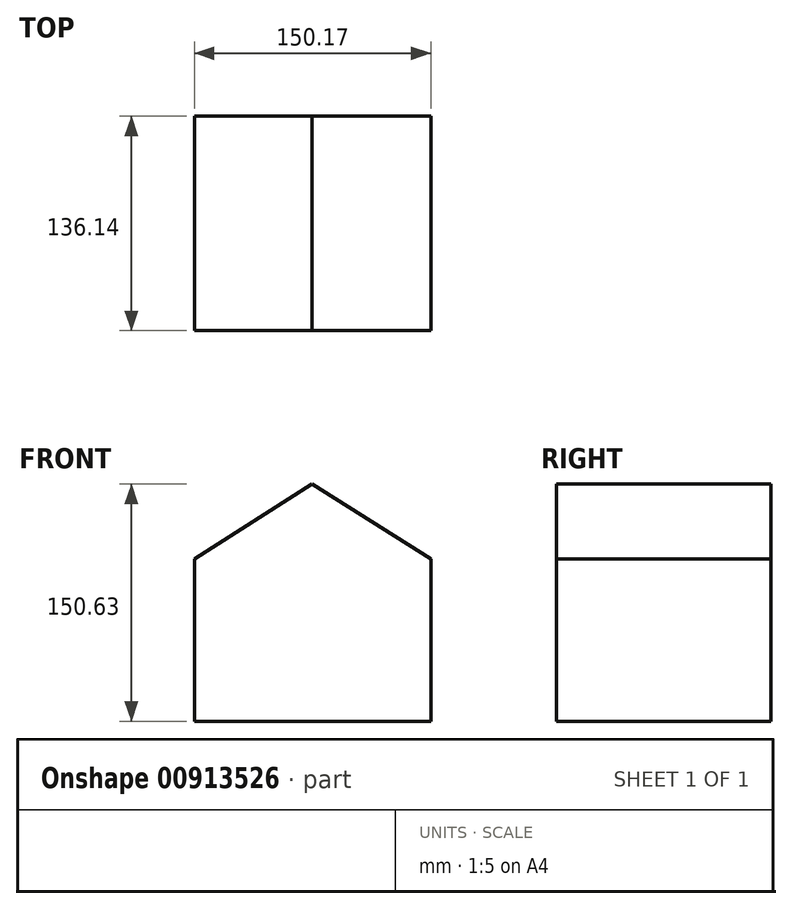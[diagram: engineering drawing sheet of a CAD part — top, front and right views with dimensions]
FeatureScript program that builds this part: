
annotation { "Feature Type Name" : "Feature", "Feature Type Description" : "" }
export const myFeature = defineFeature(function(context is Context, id is Id, definition is map)
    precondition{}
    {
        {
            var Q0;
            Q0=qCreatedBy(makeId("Front.planeOp"),FACE);
            var sketch = newSketch(context, id + "F0", { "sketchPlane" : qUnion([Q0])});
            skLineSegment(sketch, "E0", {"start": v(-74.86, -74.86) * mm, "end": v(75.31, -74.86) * mm});
            skLineSegment(sketch, "E1", {"start": v(75.31, 28.27) * mm, "end": v(75.31, -74.86) * mm});
            skLineSegment(sketch, "E2", {"start": v(75.31, 28.27) * mm, "end": v(0, 75.77) * mm});
            skLineSegment(sketch, "E3", {"start": v(0, 75.77) * mm, "end": v(-74.86, 28.27) * mm});
            skLineSegment(sketch, "E4", {"start": v(-74.86, 28.27) * mm, "end": v(-74.86, -74.86) * mm});
            skSolve(sketch);
        }
        {
            var Q0;
            Q0 = qSketchRegion(id + "F0", true);
            extrude(context, id + "F1", {"entities" : qUnion([Q0]), "depth" : 136.14 * mm, "offsetDistance" : 25.4 * mm});
        }
    });
